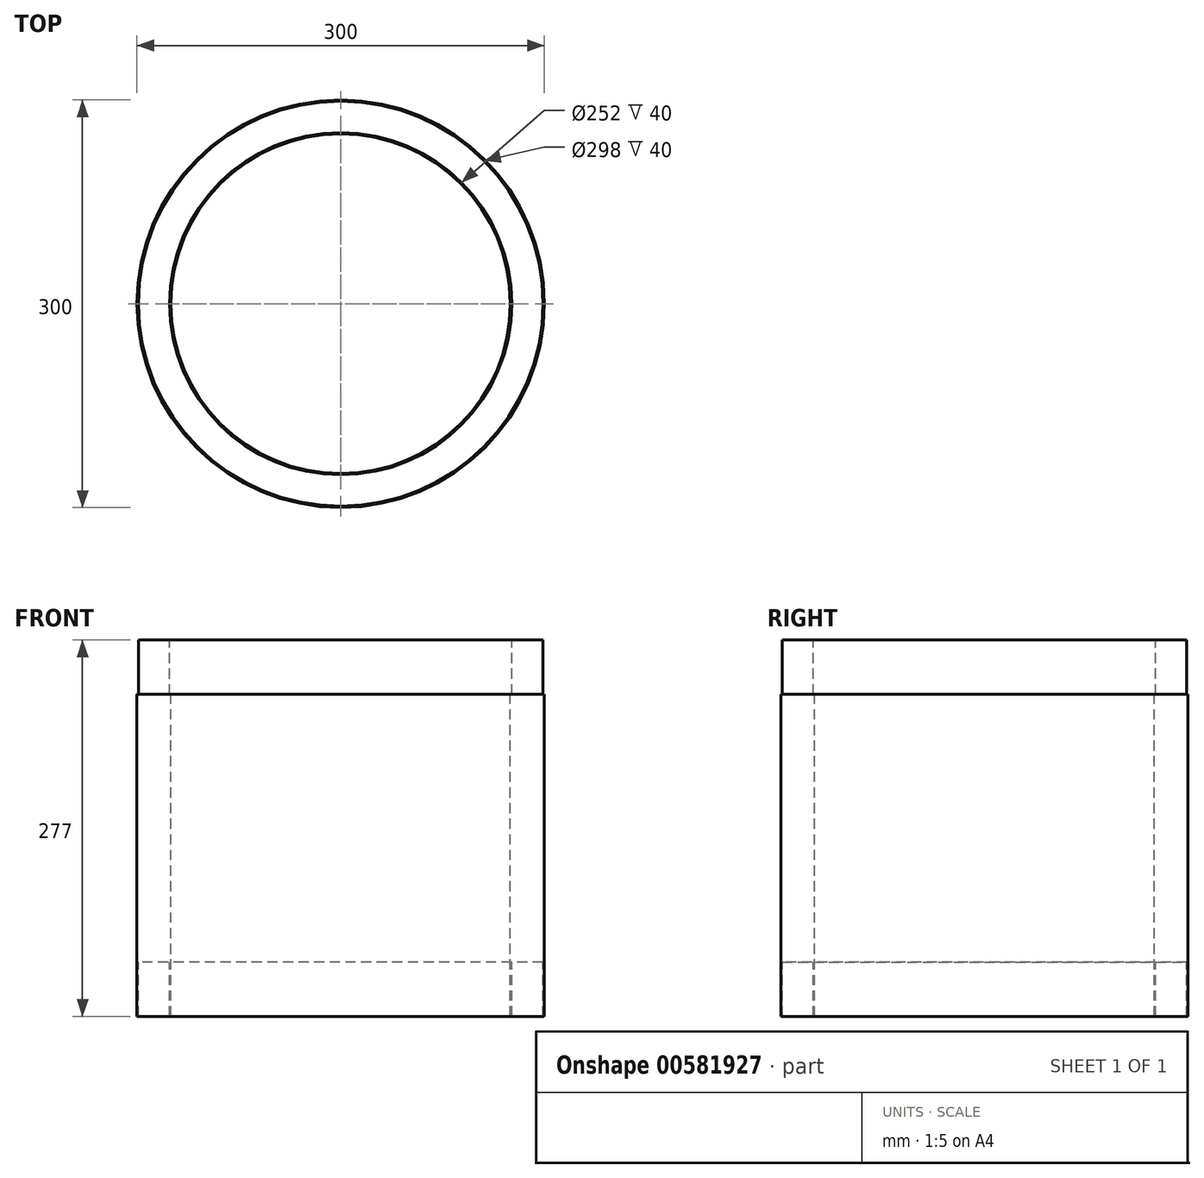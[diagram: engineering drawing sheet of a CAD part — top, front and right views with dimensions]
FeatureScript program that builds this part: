
annotation { "Feature Type Name" : "Feature", "Feature Type Description" : "" }
export const myFeature = defineFeature(function(context is Context, id is Id, definition is map)
    precondition{}
    {
        {
            var Q0;
            Q0=qCreatedBy(makeId("Front.planeOp"),FACE);
            var sketch = newSketch(context, id + "F0", { "sketchPlane" : qUnion([Q0])});
            skLineSegment(sketch, "E0", {"start": v(0, 345.75) * mm, "end": v(0, -558.03) * mm, "construction": true});
            skLineSegment(sketch, "E1", {"start": v(-125, -518.84) * mm, "end": v(-125, -281.84) * mm});
            skLineSegment(sketch, "E2", {"start": v(-125, -281.84) * mm, "end": v(-126, -281.84) * mm});
            skLineSegment(sketch, "E3", {"start": v(-126, -281.84) * mm, "end": v(-126, -241.84) * mm});
            skLineSegment(sketch, "E4", {"start": v(-126, -241.84) * mm, "end": v(-149, -241.84) * mm});
            skLineSegment(sketch, "E5", {"start": v(-149, -241.84) * mm, "end": v(-149, -281.84) * mm});
            skLineSegment(sketch, "E6", {"start": v(-149, -281.84) * mm, "end": v(-150, -281.84) * mm});
            skLineSegment(sketch, "E7", {"start": v(-150, -281.84) * mm, "end": v(-150, -518.84) * mm});
            skLineSegment(sketch, "E8", {"start": v(-150, -518.84) * mm, "end": v(-149, -518.84) * mm});
            skLineSegment(sketch, "E9", {"start": v(-149, -518.84) * mm, "end": v(-149, -478.84) * mm});
            skLineSegment(sketch, "E10", {"start": v(-149, -478.84) * mm, "end": v(-126, -478.84) * mm});
            skLineSegment(sketch, "E11", {"start": v(-126, -478.84) * mm, "end": v(-126, -518.84) * mm});
            skLineSegment(sketch, "E12", {"start": v(-126, -518.84) * mm, "end": v(-125, -518.84) * mm});
            skSolve(sketch);
        }
        {
            var Q0;
            Q0=qSketchRegion(id+"F0",true);
            var Q1;
            Q1=sQuery(id+"F0.wireOp",EDGE,"E0");
            revolve(context, id + "F1", {"entities" : qUnion([Q0]), "axis" : qUnion([Q1]), "revolveType" : RevolveType.FULL});
        }
    });
